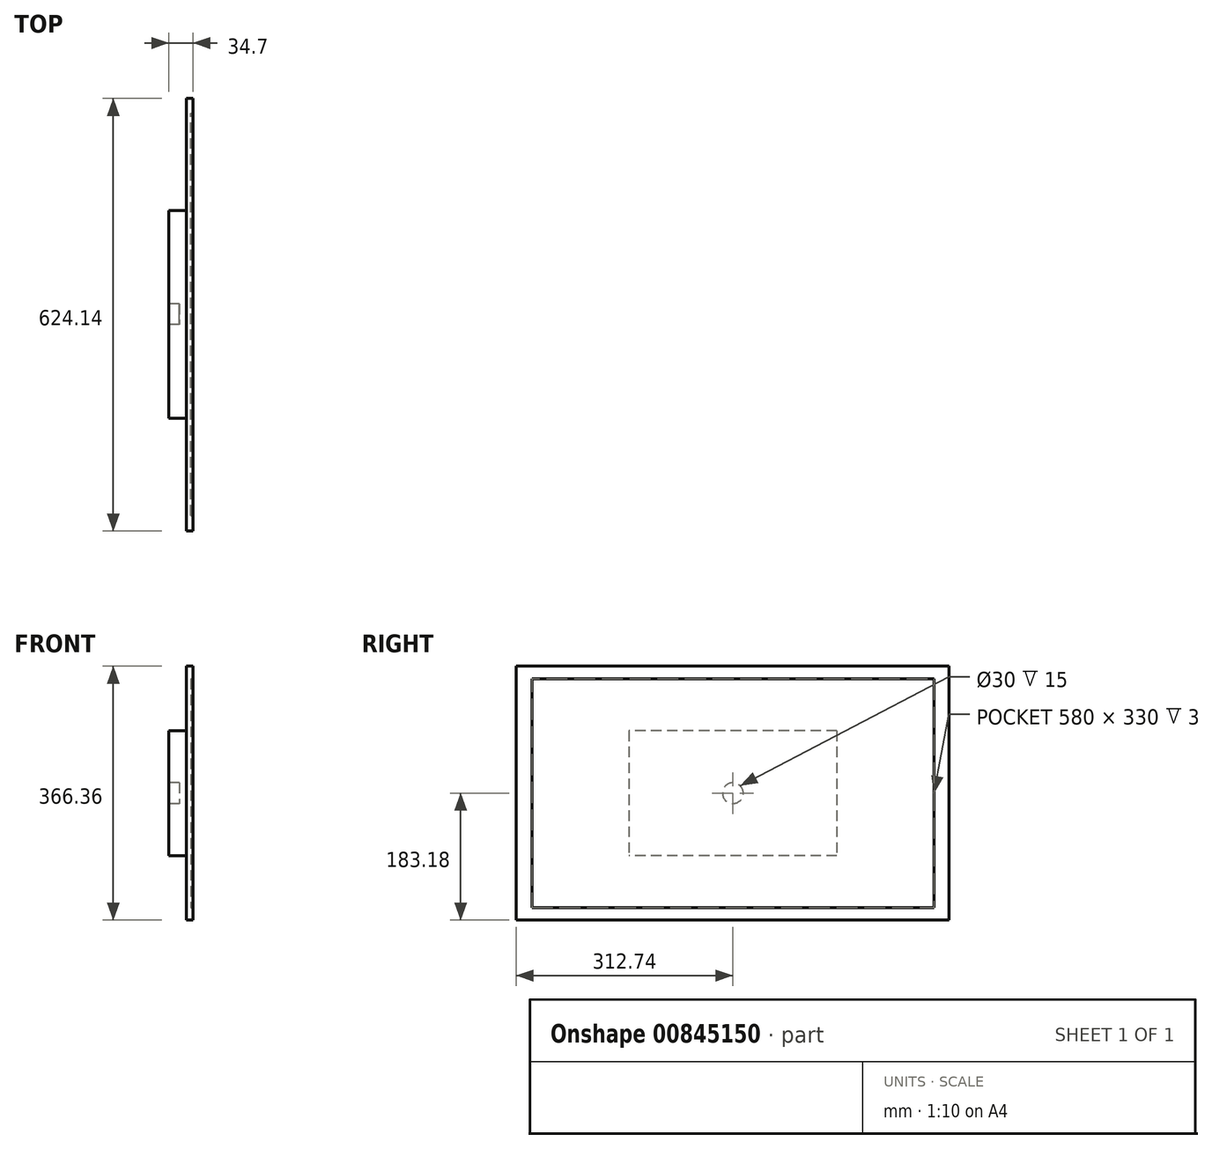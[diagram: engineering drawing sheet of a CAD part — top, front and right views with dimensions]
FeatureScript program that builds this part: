
annotation { "Feature Type Name" : "Feature", "Feature Type Description" : "" }
export const myFeature = defineFeature(function(context is Context, id is Id, definition is map)
    precondition{}
    {
        {
            var Q0;
            Q0=qCreatedBy(makeId("Right.planeOp"),FACE);
            var sketch = newSketch(context, id + "F0", { "sketchPlane" : qUnion([Q0])});
            skLineSegment(sketch, "E0.bottom", {"start": v(-312.74, 183.18) * mm, "end": v(311.4, 183.18) * mm});
            skLineSegment(sketch, "E0.top", {"start": v(-312.74, -183.18) * mm, "end": v(311.4, -183.18) * mm});
            skLineSegment(sketch, "E0.left", {"start": v(-312.74, 183.18) * mm, "end": v(-312.74, -183.18) * mm});
            skLineSegment(sketch, "E0.right", {"start": v(311.4, 183.18) * mm, "end": v(311.4, -183.18) * mm});
            skSolve(sketch);
        }
        {
            var Q0;
            Q0=makeQuery(id+"F0.imprint","IMPRINT",FACE,{"disambiguationData":[TD([[makeQuery(id+"F0.imprint","IMPRINT",EDGE,{"derivedFrom":sQuery(id+"F0.wireOp",EDGE,"E0.bottom")}),-1.0]])]});
            extrude(context, id + "F1", {"entities" : qUnion([Q0]), "depth" : 9.3 * mm, "offsetDistance" : 25.4 * mm});
        }
        {
            var Q0;
            Q0=makeQuery(id+"F1.opExtrude","CAP_FACE",FACE,{"disambiguationData":[OSD([sQuery(id+"F0.wireOp",EDGE,"E0.bottom"),sQuery(id+"F0.wireOp",EDGE,"E0.top"),sQuery(id+"F0.wireOp",EDGE,"E0.left"),sQuery(id+"F0.wireOp",EDGE,"E0.right")])],"isStart":false});
            var sketch = newSketch(context, id + "F2", { "sketchPlane" : qUnion([Q0])});
            skLineSegment(sketch, "E1.bottom", {"start": v(-290, 165) * mm, "end": v(290, 165) * mm});
            skLineSegment(sketch, "E1.top", {"start": v(-290, -165) * mm, "end": v(290, -165) * mm});
            skLineSegment(sketch, "E1.left", {"start": v(-290, 165) * mm, "end": v(-290, -165) * mm});
            skLineSegment(sketch, "E1.right", {"start": v(290, 165) * mm, "end": v(290, -165) * mm});
            skSolve(sketch);
        }
        {
            var Q0;
            Q0=makeQuery(id+"F2.imprint","IMPRINT",FACE,{"disambiguationData":[TD([[makeQuery(id+"F2.imprint","IMPRINT",EDGE,{"derivedFrom":sQuery(id+"F2.wireOp",EDGE,"E1.bottom")}),-1.0]])]});
            extrude(context, id + "F3", {"entities" : qUnion([Q0]), "operationType" : NewBodyOperationType.REMOVE, "oppositeDirection" : true, "depth" : 3 * mm, "offsetDistance" : 25.4 * mm});
        }
        {
            var Q0;
            Q0=qCreatedBy(makeId("Right.planeOp"),FACE);
            var sketch = newSketch(context, id + "F4", { "sketchPlane" : qUnion([Q0])});
            skLineSegment(sketch, "E2.bottom", {"start": v(150, 90) * mm, "end": v(-150, 90) * mm});
            skLineSegment(sketch, "E2.top", {"start": v(150, -90) * mm, "end": v(-150, -90) * mm});
            skLineSegment(sketch, "E2.left", {"start": v(150, 90) * mm, "end": v(150, -90) * mm});
            skLineSegment(sketch, "E2.right", {"start": v(-150, 90) * mm, "end": v(-150, -90) * mm});
            skSolve(sketch);
        }
        {
            var Q0;
            Q0=makeQuery(id+"F4.imprint","IMPRINT",FACE,{"disambiguationData":[TD([[makeQuery(id+"F4.imprint","IMPRINT",EDGE,{"derivedFrom":sQuery(id+"F4.wireOp",EDGE,"E2.bottom")}),1.0]])]});
            extrude(context, id + "F5", {"entities" : qUnion([Q0]), "operationType" : NewBodyOperationType.ADD, "oppositeDirection" : true, "depth" : 25.4 * mm, "offsetDistance" : 25.4 * mm});
        }
        {
            var Q0;
            Q0=makeQuery(id+"F5.opExtrude","CAP_FACE",FACE,{"disambiguationData":[OSD([sQuery(id+"F4.wireOp",EDGE,"E2.bottom"),sQuery(id+"F4.wireOp",EDGE,"E2.top"),sQuery(id+"F4.wireOp",EDGE,"E2.left"),sQuery(id+"F4.wireOp",EDGE,"E2.right")])],"isStart":false});
            var sketch = newSketch(context, id + "F6", { "sketchPlane" : qUnion([Q0])});
            skPoint(sketch, "E3.centerSnap0", {"position": v(0, 90) * mm});
            skCircle(sketch, "E4", {"center": v(0, 0) * mm, "radius": 15 * mm});
            skSolve(sketch);
        }
        {
            var Q0;
            Q0=makeQuery(id+"F6.imprint","IMPRINT",FACE,{"disambiguationData":[TD([[makeQuery(id+"F6.imprint","IMPRINT",EDGE,{"derivedFrom":sQuery(id+"F6.wireOp",EDGE,"E4")}),1.0]])]});
            extrude(context, id + "F7", {"entities" : qUnion([Q0]), "operationType" : NewBodyOperationType.REMOVE, "oppositeDirection" : true, "depth" : 15 * mm, "offsetDistance" : 25 * mm});
        }
    });
